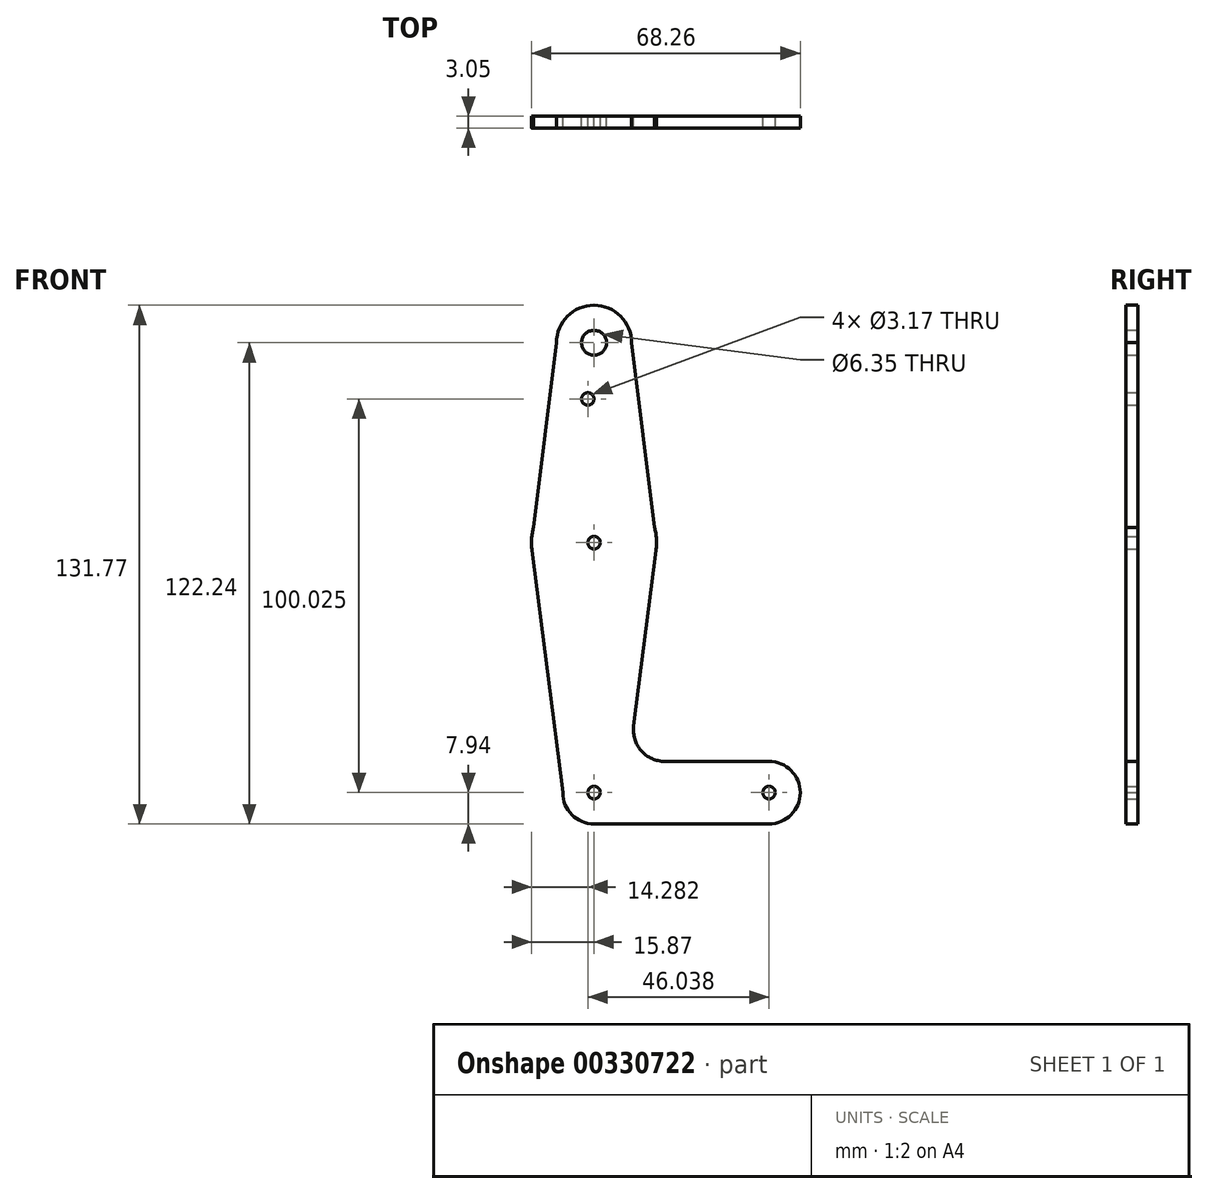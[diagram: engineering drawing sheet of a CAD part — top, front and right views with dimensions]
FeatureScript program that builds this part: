
annotation { "Feature Type Name" : "Feature", "Feature Type Description" : "" }
export const myFeature = defineFeature(function(context is Context, id is Id, definition is map)
    precondition{}
    {
        {
            var Q0;
            Q0=qCreatedBy(makeId("Front.planeOp"),FACE);
            var sketch = newSketch(context, id + "F0", { "sketchPlane" : qUnion([Q0])});
            skLineSegment(sketch, "E0", {"start": v(0, 0) * mm, "end": v(0, 114.3) * mm, "construction": true});
            skLineSegment(sketch, "E1", {"start": v(0, 0) * mm, "end": v(44.45, 0) * mm, "construction": true});
            skCircle(sketch, "E2", {"center": v(0, 114.3) * mm, "radius": 9.53 * mm});
            skCircle(sketch, "E3", {"center": v(0, 63.5) * mm, "radius": 15.88 * mm});
            skCircle(sketch, "E4", {"center": v(0, 0) * mm, "radius": 7.94 * mm});
            skCircle(sketch, "E5", {"center": v(44.45, 0) * mm, "radius": 7.94 * mm});
            skLineSegment(sketch, "E6", {"start": v(9.52, 114.3) * mm, "end": v(15.88, 63.5) * mm});
            skLineSegment(sketch, "E7", {"start": v(-9.52, 114.3) * mm, "end": v(-15.88, 63.5) * mm});
            skLineSegment(sketch, "E8", {"start": v(-15.75, 61.5) * mm, "end": v(-7.94, 0) * mm});
            skLineSegment(sketch, "E9", {"start": v(15.75, 61.5) * mm, "end": v(10.08, 16.89) * mm});
            skLineSegment(sketch, "E10", {"start": v(17.97, 7.94) * mm, "end": v(44.45, 7.94) * mm});
            skLineSegment(sketch, "E11", {"start": v(0, -7.94) * mm, "end": v(44.45, -7.94) * mm});
            skCircle(sketch, "E12", {"center": v(0, 63.5) * mm, "radius": 1.59 * mm});
            skCircle(sketch, "E13", {"center": v(0, 0) * mm, "radius": 1.59 * mm});
            skCircle(sketch, "E14", {"center": v(44.45, 0) * mm, "radius": 1.59 * mm});
            skCircle(sketch, "E15", {"center": v(-1.59, 100.03) * mm, "radius": 1.59 * mm});
            skArc(sketch, "E16.filletArc", {"start": v(10.08, 16.89) * mm, "mid": v(12, 10.63) * mm, "end": v(17.97, 7.94) * mm});
            skCircle(sketch, "E17", {"center": v(0, 114.3) * mm, "radius": 3.18 * mm});
            skSolve(sketch);
        }
        {
            var Q0;
            Q0 = qSketchRegion(id + "F0", true);
            extrude(context, id + "F1", {"entities" : qUnion([Q0]), "depth" : 3.05 * mm});
        }
        {
            var Q0;
            Q0 = qSketchRegion(id + "F0", true);
            extrude(context, id + "F2", {"entities" : qUnion([Q0]), "operationType" : NewBodyOperationType.ADD, "depth" : 3.05 * mm});
        }
    });
